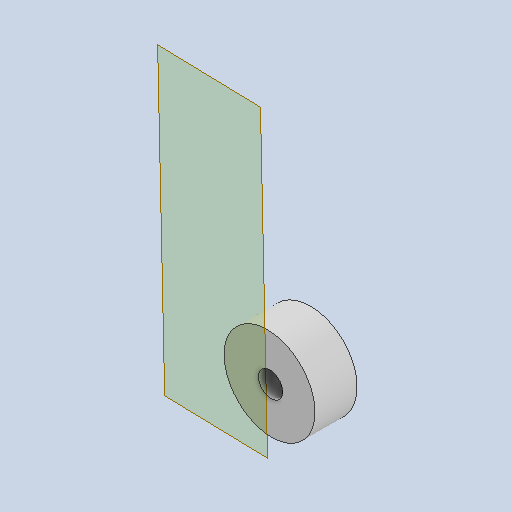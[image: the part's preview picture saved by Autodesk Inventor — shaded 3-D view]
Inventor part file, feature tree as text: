
AUTODESK INVENTOR PART (.ipt)
format: ipt  version: 2024 (Build 280153000, 153)  size: 150,528 bytes
history: native  units: mm
features: other x3, plane x2, reference x2, sketch x1, extrude x1
ambient origin geometry x8: Origin, YZ Plane, XZ Plane, XY Plane, X Axis, Y Axis, Z Axis, Center Point
bodies: Solid1 (feature_tree)
feature tree (9):
  plane  "Work Plane1"
  sketch  "Sketch1"  dims[d0=10.0mm d1=0.0mm]
  plane  "Work Plane2"
  extrude  "Extrusion1"  [1 undecoded]
  reference  "Reference1"
  reference  "Reference2"
  other  "<userpath>\Documents\Inventor\robot arm\base.iam"
  other  "base.iam"
  other  "middel arm"
note: 1 required parameter value undecoded (feature->parameter linkage not recoverable at this tier; creation-order binding heuristic only, values carry confidence <= 0.55)
